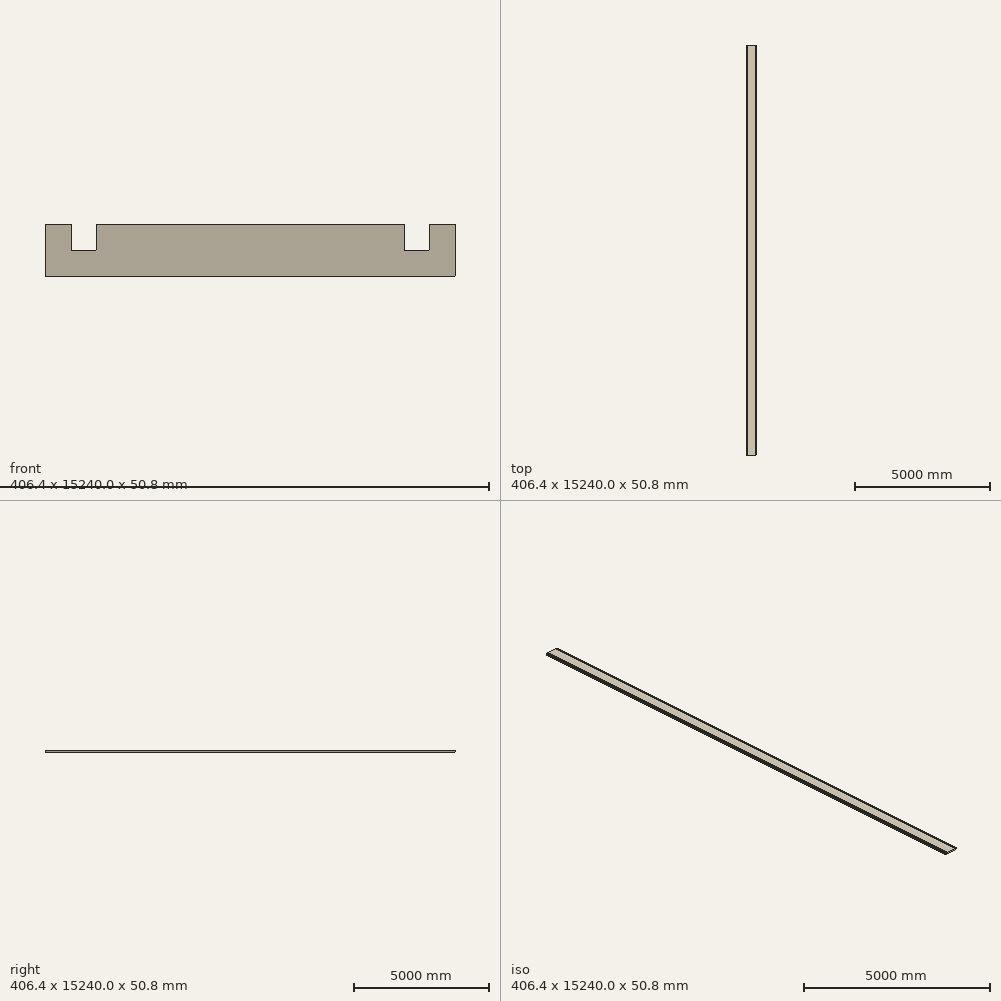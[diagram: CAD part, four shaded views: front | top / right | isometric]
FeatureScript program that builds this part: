
annotation { "Feature Type Name" : "Feature", "Feature Type Description" : "" }
export const myFeature = defineFeature(function(context is Context, id is Id, definition is map)
    precondition{}
    {
        {
            var Q0;
            Q0=qCreatedBy(makeId("Front.planeOp"),FACE);
            var sketch = newSketch(context, id + "F0", { "sketchPlane" : qUnion([Q0])});
            skLineSegment(sketch, "E0.bottom", {"start": v(0, 50.8) * mm, "end": v(25.4, 50.8) * mm});
            skLineSegment(sketch, "E0.top", {"start": v(0, 0) * mm, "end": v(406.4, 0) * mm});
            skLineSegment(sketch, "E0.left", {"start": v(0, 50.8) * mm, "end": v(0, 0) * mm});
            skLineSegment(sketch, "E0.right", {"start": v(406.4, 50.8) * mm, "end": v(406.4, 0) * mm});
            skLineSegment(sketch, "E1.top", {"start": v(25.4, 25.4) * mm, "end": v(50.8, 25.4) * mm});
            skLineSegment(sketch, "E1.left", {"start": v(25.4, 50.8) * mm, "end": v(25.4, 25.4) * mm});
            skLineSegment(sketch, "E1.right", {"start": v(50.8, 50.8) * mm, "end": v(50.8, 25.4) * mm});
            skLineSegment(sketch, "E2.top", {"start": v(355.6, 25.4) * mm, "end": v(381, 25.4) * mm});
            skLineSegment(sketch, "E2.left", {"start": v(355.6, 50.8) * mm, "end": v(355.6, 25.4) * mm});
            skLineSegment(sketch, "E2.right", {"start": v(381, 50.8) * mm, "end": v(381, 25.4) * mm});
            skLineSegment(sketch, "E3.trimOffspring", {"start": v(50.8, 50.8) * mm, "end": v(355.6, 50.8) * mm});
            skLineSegment(sketch, "E4.trimOffspring", {"start": v(381, 50.8) * mm, "end": v(406.4, 50.8) * mm});
            skSolve(sketch);
        }
        {
            var Q0;
            Q0 = qSketchRegion(id + "F0", true);
            extrude(context, id + "F1", {"entities" : qUnion([Q0]), "depth" : 15240 * mm});
        }
    });
